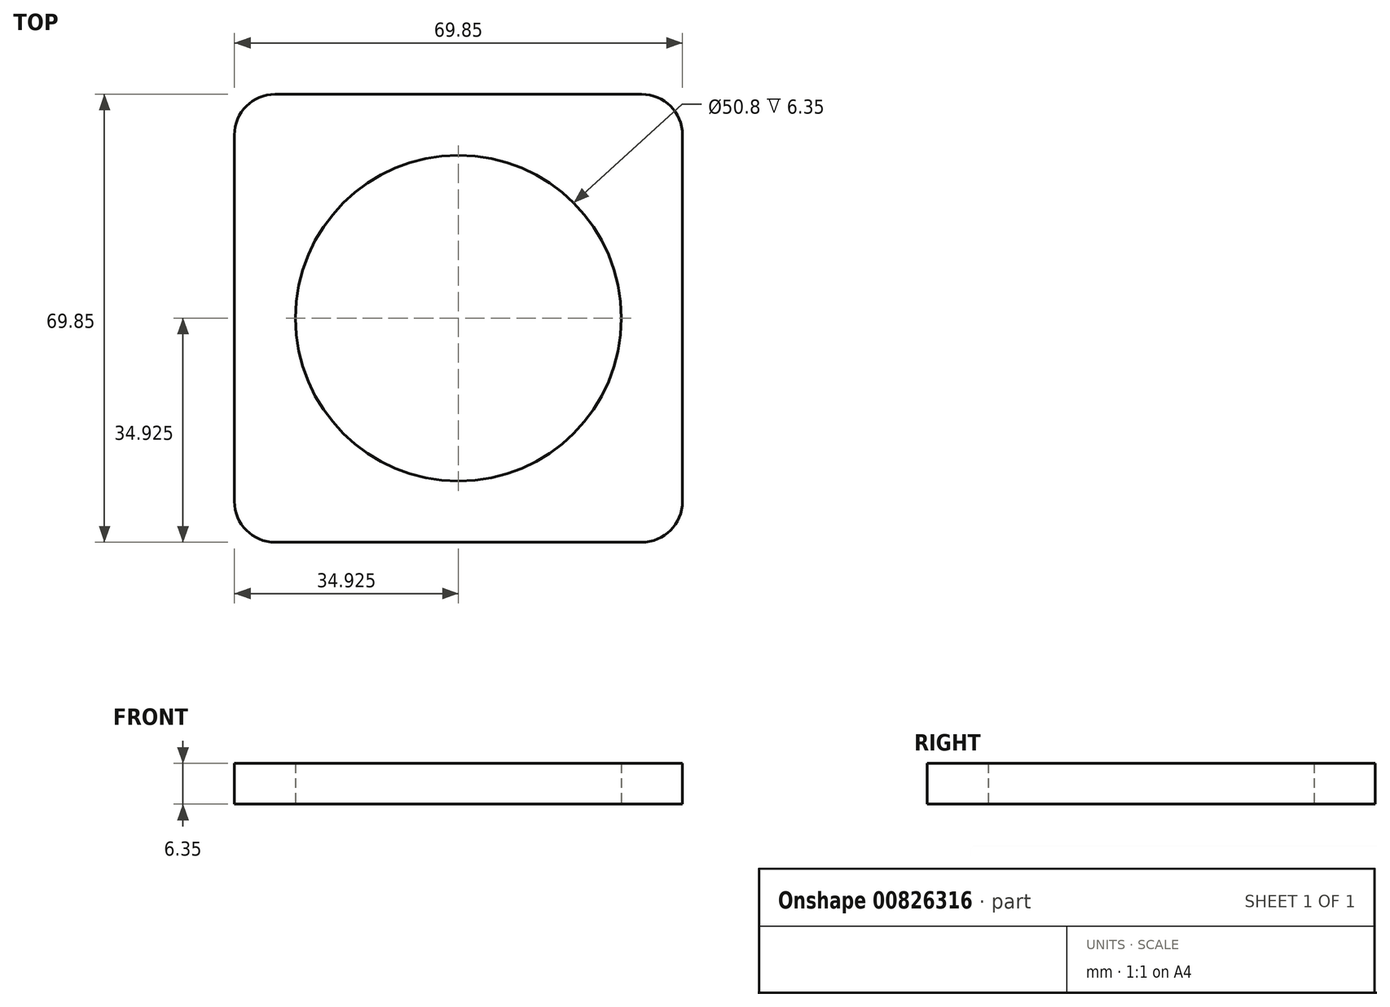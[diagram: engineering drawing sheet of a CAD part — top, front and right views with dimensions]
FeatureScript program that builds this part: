
annotation { "Feature Type Name" : "Feature", "Feature Type Description" : "" }
export const myFeature = defineFeature(function(context is Context, id is Id, definition is map)
    precondition{}
    {
        {
            var Q0;
            Q0=qCreatedBy(makeId("Top.planeOp"),FACE);
            var sketch = newSketch(context, id + "F0", { "sketchPlane" : qUnion([Q0])});
            skLineSegment(sketch, "E0.bottom", {"start": v(6.35, 0) * mm, "end": v(63.5, 0) * mm});
            skLineSegment(sketch, "E0.top", {"start": v(6.35, -69.85) * mm, "end": v(63.5, -69.85) * mm});
            skLineSegment(sketch, "E0.left", {"start": v(0, -6.35) * mm, "end": v(0, -63.5) * mm});
            skLineSegment(sketch, "E0.right", {"start": v(69.85, -6.35) * mm, "end": v(69.85, -63.5) * mm});
            skPoint(sketch, "E1.visualSharp", {"position": v(0, 0) * mm});
            skArc(sketch, "E1.filletArc", {"start": v(6.35, 0) * mm, "mid": v(1.86, -1.86) * mm, "end": v(0, -6.35) * mm});
            skPoint(sketch, "E2.visualSharp", {"position": v(0, -69.85) * mm});
            skArc(sketch, "E2.filletArc", {"start": v(0, -63.5) * mm, "mid": v(1.86, -68) * mm, "end": v(6.35, -69.85) * mm});
            skPoint(sketch, "E3.visualSharp", {"position": v(69.85, -69.85) * mm});
            skArc(sketch, "E3.filletArc", {"start": v(63.5, -69.85) * mm, "mid": v(68, -68) * mm, "end": v(69.85, -63.5) * mm});
            skPoint(sketch, "E4.visualSharp", {"position": v(69.85, 0) * mm});
            skArc(sketch, "E4.filletArc", {"start": v(69.85, -6.35) * mm, "mid": v(68, -1.86) * mm, "end": v(63.5, 0) * mm});
            skCircle(sketch, "E5", {"center": v(34.93, -34.92) * mm, "radius": 25.4 * mm});
            skPoint(sketch, "E5.centerSnap0", {"position": v(34.92, 0) * mm});
            skLineSegment(sketch, "E6", {"start": v(34.92, 0) * mm, "end": v(34.92, -34.92) * mm, "construction": true});
            skLineSegment(sketch, "E7", {"start": v(69.85, -34.92) * mm, "end": v(34.93, -34.92) * mm, "construction": true});
            skSolve(sketch);
        }
        {
            var Q0;
            Q0=makeQuery(id+"F0.imprint","IMPRINT",FACE,{"disambiguationData":[TD([[makeQuery(id+"F0.imprint","IMPRINT",EDGE,{"derivedFrom":sQuery(id+"F0.wireOp",EDGE,"E0.bottom")}),-1.0]])]});
            extrude(context, id + "F1", {"entities" : qUnion([Q0]), "depth" : 6.35 * mm, "offsetDistance" : 25.4 * mm});
        }
    });
